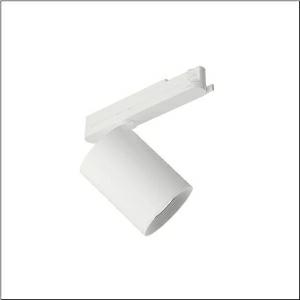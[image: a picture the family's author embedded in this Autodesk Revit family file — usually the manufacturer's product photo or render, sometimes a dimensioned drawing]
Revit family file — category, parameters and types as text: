
# Revit family: spot_21_51se13dbb5b
name_source: partatom
category: Lighting Fixtures
units: mm (PartAtom-declared; Revit-internal decimal feet)

## family parameters
Cut with Voids When Loaded = No
Host = Face
Light Source = No
Part Type = Normal
Room Calculation Point = No
Round Connector Dimension = Use Diameter
Shared = No

## types (1)
- --- (1 x LED, 5160 lm, 42.4 W, 3000K)
    Apparent Load = 42 VA
    CIE Flux Codes = 95 98 99 100 100
    Color Rendering = 90
    Color Temperature = 3000K
    Default Elevation = 1800 mm
    Description = Spot 21, directional spotlight, light control with lens, of PMMA, LED rated luminous flux: 5.120lm, light colour: 930, control gear: ECG Multilumen, with 3-phase adapter, mains connection: 220..240V, AC, 50/60Hz, of aluminium, traffic white (RAL 9016), length: 253mm, diameter: 105mm, protection rating (complete): IP20, insulation class (complete): insulation class I (protective earthing), certification: CE, impact resistance: IK02, permissible ambient temperature for indoor applications: -20..+40°C, packaging unit: 1 piece
    Height = 175 mm
    Lamp = 1 x LED
    Lamp Light Flux = 5160 lm
    Lamp Power = 42.4 W
    Lamp count = 1
    Length = 105 mm
    Luminous efficacy = 122 lm/W
    Manufacturer = Siteco
    ModVariant = No
    Model = 51SE13DBB5B
    Mounting Place = Ceiling
    Mounting Type = Pendant
    Number of Poles = 1
    OnlyDefault = Yes
    Power Factor = 1
    Product Name = Spot 21
    Product group = directional spotlight
    ProductGroupID = 904
    Protection Class = Protection class I
    Protection Degree = IP 20
    RLX_Detail_Level = 1
    RlxData = <blob elided: 17657 chars, md5=d5820dbc>
    Socket = socket
    Standby Power = 0 W
    System Light Flux = 5160 lm
    System Power = 42 W
    Type Comments = factory setting: luminous flux: 100 % | (ON | ON | ON | ON) | 1050 mA
    Type Image = l_1003976.jpg
    URL = http://relux.com
    VarID = @adj_053309
    Voltage = 0 V
    Weight = 0.00 kg
    Width = 0 mm  [stored 0 ft]

note: [stored X ft] marks values corroborated as IEEE doubles in the binary element streams (Revit-internal decimal feet)

## geometry (parser evidence)
native form markers: Blend x4, Sweep x12
no freeform markers — native parametric forms only
